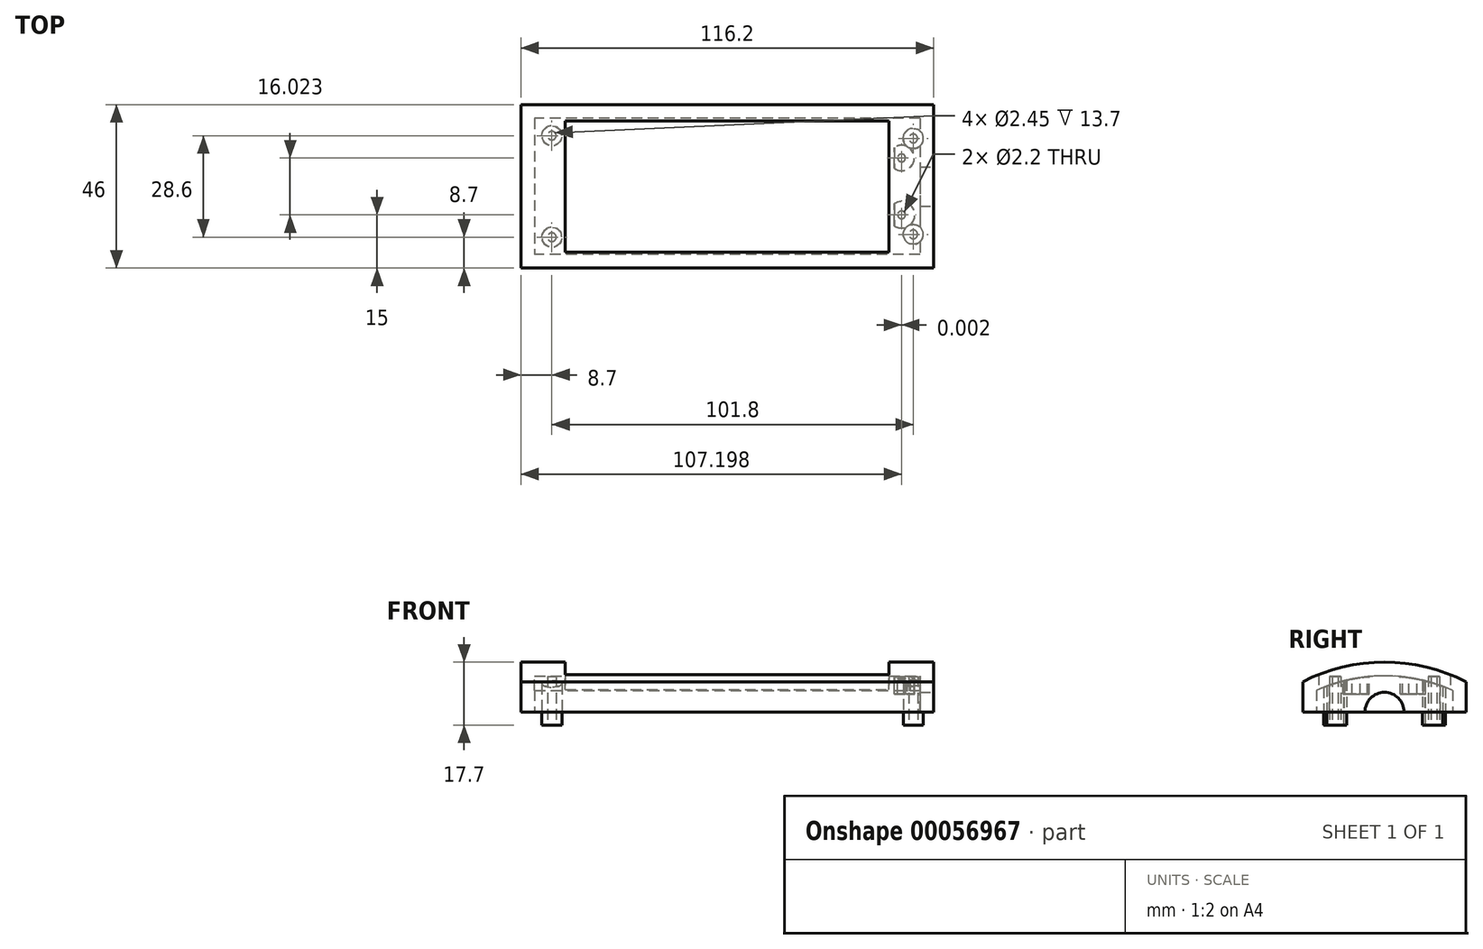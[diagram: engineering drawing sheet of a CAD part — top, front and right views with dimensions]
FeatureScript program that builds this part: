
annotation { "Feature Type Name" : "Feature", "Feature Type Description" : "" }
export const myFeature = defineFeature(function(context is Context, id is Id, definition is map)
    precondition{}
    {
        {
            var Q0;
            Q0=qCreatedBy(makeId("Top.planeOp"),FACE);
            var sketch = newSketch(context, id + "F0", { "sketchPlane" : qUnion([Q0])});
            skLineSegment(sketch, "E0.rect.bottom", {"start": v(58.1, 23) * mm, "end": v(-58.1, 23) * mm});
            skLineSegment(sketch, "E0.rect.top", {"start": v(58.1, -23) * mm, "end": v(-58.1, -23) * mm});
            skLineSegment(sketch, "E0.rect.left", {"start": v(58.1, 23) * mm, "end": v(58.1, -23) * mm});
            skLineSegment(sketch, "E0.rect.right", {"start": v(-58.1, 23) * mm, "end": v(-58.1, -23) * mm});
            skPoint(sketch, "E0.rect.middle", {"position": v(0, 0) * mm});
            skLineSegment(sketch, "E1.rect.bottom", {"start": v(45.6, 18.5) * mm, "end": v(-45.6, 18.5) * mm});
            skLineSegment(sketch, "E1.rect.top", {"start": v(45.6, -18.5) * mm, "end": v(-45.6, -18.5) * mm});
            skLineSegment(sketch, "E1.rect.left", {"start": v(45.6, 18.5) * mm, "end": v(45.6, -18.5) * mm});
            skLineSegment(sketch, "E1.rect.right", {"start": v(-45.6, 18.5) * mm, "end": v(-45.6, -18.5) * mm});
            skSolve(sketch);
        }
        {
            var Q0;
            Q0=makeQuery(id+"F0.imprint","IMPRINT",FACE,{"disambiguationData":[TD([[makeQuery(id+"F0.imprint","IMPRINT",EDGE,{"derivedFrom":sQuery(id+"F0.wireOp",EDGE,"E0.rect.bottom")}),1.0]])]});
            var Q1;
            Q1=makeQuery(id+"F0.imprint","IMPRINT",FACE,{"disambiguationData":[TD([[makeQuery(id+"F0.imprint","IMPRINT",EDGE,{"derivedFrom":sQuery(id+"F0.wireOp",EDGE,"E1.rect.bottom")}),1.0]])]});
            extrude(context, id + "F1", {"entities" : qUnion([Q0, Q1]), "depth" : 14 * mm});
        }
        {
            var Q0;
            Q0=makeQuery(id+"F1.opExtrude","SWEPT_FACE",FACE,{"disambiguationData":[OSD([sQuery(id+"F0.wireOp",EDGE,"E0.rect.left")])]});
            var sketch = newSketch(context, id + "F2", { "sketchPlane" : qUnion([Q0])});
            skLineSegment(sketch, "E2", {"start": v(-23, 0) * mm, "end": v(-23, 8.5) * mm, "construction": true});
            skLineSegment(sketch, "E3", {"start": v(-23, 8.5) * mm, "end": v(23, 8.5) * mm, "construction": true});
            skLineSegment(sketch, "E4", {"start": v(23, 8.5) * mm, "end": v(23, 0) * mm, "construction": true});
            skLineSegment(sketch, "E5", {"start": v(23, 0) * mm, "end": v(-23, 0) * mm, "construction": true});
            skLineSegment(sketch, "E6.0", {"start": v(23, 14) * mm, "end": v(-23, 14) * mm, "construction": true});
            skLineSegment(sketch, "E7", {"start": v(0, 8.5) * mm, "end": v(0, 15.93) * mm, "construction": true});
            skPoint(sketch, "E7.endSnap0", {"position": v(0, 14) * mm});
            skArc(sketch, "E8", {"start": v(23, 8.5) * mm, "mid": v(0, 14) * mm, "end": v(-23, 8.5) * mm});
            skLineSegment(sketch, "E9", {"start": v(-23, 8.5) * mm, "end": v(-26.27, 8.5) * mm});
            skLineSegment(sketch, "E10", {"start": v(-26.27, 8.5) * mm, "end": v(-26.27, 18.5) * mm});
            skLineSegment(sketch, "E11", {"start": v(-26.27, 18.5) * mm, "end": v(26.97, 18.5) * mm});
            skLineSegment(sketch, "E12", {"start": v(26.97, 18.5) * mm, "end": v(26.97, 8.2) * mm});
            skLineSegment(sketch, "E13", {"start": v(26.97, 8.2) * mm, "end": v(23, 8.5) * mm});
            skSolve(sketch);
        }
        {
            var Q0;
            {var subQ4=sQuery(id+"F2.wireOp",EDGE,"E9");Q0=makeQuery(id+"F2.imprint","IMPRINT",FACE,{"disambiguationData":[TD([[makeQuery(id+"F2.imprint","IMPRINT",EDGE,{"derivedFrom":subQ4}),-1.0]])]});}
            var Q1;
            {var subQ0=sQuery(id+"F2.wireOp",EDGE,"E8");var subQ1=sQuery(id+"F0.wireOp",EDGE,"E0.rect.left");var subQ4=makeQuery(id+"F1.opExtrude","CAP_EDGE",EDGE,{"disambiguationData":[OSD([subQ1])],"isStart":false});var subQ5=makeQuery(id+"F2.imprint","INTERSECT",VERTEX,{"derivedFrom":[subQ4,subQ0]});Q1=makeQuery(id+"F2.imprint","IMPRINT",FACE,{"disambiguationData":[TD([[makeQuery(id+"F2.imprint","IMPRINT",EDGE,{"disambiguationData":[TD([[subQ5,-1.0]])],"derivedFrom":subQ4}),1.0]])]});}
            var Q2;
            {var subQ0=sQuery(id+"F2.wireOp",EDGE,"E8");var subQ1=sQuery(id+"F0.wireOp",EDGE,"E0.rect.left");var subQ4=makeQuery(id+"F1.opExtrude","CAP_EDGE",EDGE,{"disambiguationData":[OSD([subQ1])],"isStart":false});var subQ5=makeQuery(id+"F2.imprint","INTERSECT",VERTEX,{"derivedFrom":[subQ4,subQ0]});Q2=makeQuery(id+"F2.imprint","IMPRINT",FACE,{"disambiguationData":[TD([[makeQuery(id+"F2.imprint","IMPRINT",EDGE,{"disambiguationData":[TD([[subQ5,1.0]])],"derivedFrom":subQ4}),1.0]])]});}
            extrude(context, id + "F3", {"entities" : qUnion([Q0, Q1, Q2]), "operationType" : NewBodyOperationType.REMOVE, "endBound" : BoundingType.THROUGH_ALL, "oppositeDirection" : true, "depth" : 25 * mm});
        }
        {
            var Q0;
            Q0=makeQuery(id+"F1.opExtrude","CAP_FACE",FACE,{"disambiguationData":[OSD([sQuery(id+"F0.wireOp",EDGE,"E0.rect.bottom"),sQuery(id+"F0.wireOp",EDGE,"E0.rect.top"),sQuery(id+"F0.wireOp",EDGE,"E0.rect.left"),sQuery(id+"F0.wireOp",EDGE,"E0.rect.right")])],"isStart":true});
            shell(context, id + "F4", {"entities" : qUnion([Q0]), "thickness" : 3.85 * mm});
        }
        {
            var Q0;
            Q0=qCreatedBy(makeId("Top.planeOp"),FACE);
            var sketch = newSketch(context, id + "F5", { "sketchPlane" : qUnion([Q0])});
            skPoint(sketch, "E14.4", {"position": v(0, 0) * mm});
            skLineSegment(sketch, "E14.5", {"start": v(45.6, 18.5) * mm, "end": v(-45.6, 18.5) * mm});
            skLineSegment(sketch, "E14.6", {"start": v(45.6, -18.5) * mm, "end": v(-45.6, -18.5) * mm});
            skLineSegment(sketch, "E14.7", {"start": v(45.6, 18.5) * mm, "end": v(45.6, -18.5) * mm});
            skLineSegment(sketch, "E14.8", {"start": v(-45.6, 18.5) * mm, "end": v(-45.6, -18.5) * mm});
            skPoint(sketch, "E14.9", {"position": v(0, 0) * mm});
            skSolve(sketch);
        }
        {
            var Q0;
            Q0=makeQuery(id+"F5.imprint","IMPRINT",FACE,{"disambiguationData":[TD([[makeQuery(id+"F5.imprint","IMPRINT",EDGE,{"derivedFrom":sQuery(id+"F5.wireOp",EDGE,"E14.5")}),1.0]])]});
            extrude(context, id + "F6", {"entities" : qUnion([Q0]), "operationType" : NewBodyOperationType.REMOVE, "endBound" : BoundingType.THROUGH_ALL, "depth" : 25 * mm});
        }
        {
            var Q0;
            Q0=makeQuery(id+"F1.opExtrude","CAP_FACE",FACE,{"disambiguationData":[OSD([sQuery(id+"F0.wireOp",EDGE,"E0.rect.bottom"),sQuery(id+"F0.wireOp",EDGE,"E0.rect.top"),sQuery(id+"F0.wireOp",EDGE,"E0.rect.left"),sQuery(id+"F0.wireOp",EDGE,"E0.rect.right")])],"isStart":true});
            var sketch = newSketch(context, id + "F7", { "sketchPlane" : qUnion([Q0])});
            skLineSegment(sketch, "E15.bottom", {"start": v(-58.1, 23) * mm, "end": v(-49.4, 23) * mm, "construction": true});
            skLineSegment(sketch, "E15.top", {"start": v(-58.1, 14.3) * mm, "end": v(-49.4, 14.3) * mm, "construction": true});
            skLineSegment(sketch, "E15.left", {"start": v(-58.1, 23) * mm, "end": v(-58.1, 14.3) * mm, "construction": true});
            skLineSegment(sketch, "E15.right", {"start": v(-49.4, 23) * mm, "end": v(-49.4, 14.3) * mm, "construction": true});
            skCircle(sketch, "E16", {"center": v(-49.4, 14.3) * mm, "radius": 2.8 * mm});
            skLineSegment(sketch, "E17.bottom", {"start": v(-58.1, -23) * mm, "end": v(-49.4, -23) * mm, "construction": true});
            skLineSegment(sketch, "E17.top", {"start": v(-58.1, -14.3) * mm, "end": v(-49.4, -14.3) * mm, "construction": true});
            skLineSegment(sketch, "E17.left", {"start": v(-58.1, -23) * mm, "end": v(-58.1, -14.3) * mm, "construction": true});
            skLineSegment(sketch, "E17.right", {"start": v(-49.4, -23) * mm, "end": v(-49.4, -14.3) * mm, "construction": true});
            skCircle(sketch, "E18", {"center": v(-49.4, -14.3) * mm, "radius": 2.8 * mm});
            skLineSegment(sketch, "E19.bottom", {"start": v(58.1, 23) * mm, "end": v(52.4, 23) * mm, "construction": true});
            skLineSegment(sketch, "E19.top", {"start": v(58.1, 13.5) * mm, "end": v(52.4, 13.5) * mm, "construction": true});
            skLineSegment(sketch, "E19.left", {"start": v(58.1, 23) * mm, "end": v(58.1, 13.5) * mm, "construction": true});
            skLineSegment(sketch, "E19.right", {"start": v(52.4, 23) * mm, "end": v(52.4, 13.5) * mm, "construction": true});
            skCircle(sketch, "E20", {"center": v(52.4, 13.5) * mm, "radius": 2.8 * mm});
            skLineSegment(sketch, "E21.bottom", {"start": v(58.1, -23) * mm, "end": v(52.4, -23) * mm, "construction": true});
            skLineSegment(sketch, "E21.top", {"start": v(58.1, -13.5) * mm, "end": v(52.4, -13.5) * mm, "construction": true});
            skLineSegment(sketch, "E21.left", {"start": v(58.1, -23) * mm, "end": v(58.1, -13.5) * mm, "construction": true});
            skLineSegment(sketch, "E21.right", {"start": v(52.4, -23) * mm, "end": v(52.4, -13.5) * mm, "construction": true});
            skCircle(sketch, "E22", {"center": v(52.4, -13.5) * mm, "radius": 2.85 * mm});
            skSolve(sketch);
        }
        {
            var Q0;
            Q0 = qSketchRegion(id + "F7", true);
            var Q1;
            Q1=makeQuery(id+"F4.opShell","OFFSET_FACE",FACE,{"disambiguationData":[OSD([sQuery(id+"F2.wireOp",EDGE,"E8")])]});
            extrude(context, id + "F8", {"entities" : qUnion([Q0]), "operationType" : NewBodyOperationType.ADD, "endBound" : BoundingType.UP_TO_SURFACE, "oppositeDirection" : true, "endBoundEntityFace" : qUnion([Q1]), "depth" : 25 * mm});
        }
        {
            var Q0;
            Q0=makeQuery(id+"F1.opExtrude","SWEPT_FACE",FACE,{"disambiguationData":[OSD([sQuery(id+"F0.wireOp",EDGE,"E0.rect.left")])]});
            var sketch = newSketch(context, id + "F9", { "sketchPlane" : qUnion([Q0])});
            skCircle(sketch, "E23", {"center": v(0, 0) * mm, "radius": 5.5 * mm});
            skSolve(sketch);
        }
        {
            var Q0;
            {var subQ0=sQuery(id+"F9.wireOp",EDGE,"E23");var subQ1=makeQuery(id+"F1.opExtrude","CAP_EDGE",EDGE,{"disambiguationData":[OSD([sQuery(id+"F0.wireOp",EDGE,"E0.rect.left")])],"isStart":true});var subQ2=makeQuery(id+"F9.imprint","INTERSECT",VERTEX,{"disambiguationData":[OD(0.0)],"derivedFrom":[subQ1,subQ0]});Q0=makeQuery(id+"F9.imprint","IMPRINT",FACE,{"disambiguationData":[TD([[makeQuery(id+"F9.imprint","IMPRINT",EDGE,{"disambiguationData":[TD([[subQ2,1.0]])],"derivedFrom":subQ0}),1.0]])]});}
            var Q1;
            {var subQ0=sQuery(id+"F9.wireOp",EDGE,"E23");var subQ1=makeQuery(id+"F1.opExtrude","CAP_EDGE",EDGE,{"disambiguationData":[OSD([sQuery(id+"F0.wireOp",EDGE,"E0.rect.left")])],"isStart":true});var subQ2=makeQuery(id+"F9.imprint","INTERSECT",VERTEX,{"disambiguationData":[OD(0.0)],"derivedFrom":[subQ1,subQ0]});Q1=makeQuery(id+"F9.imprint","IMPRINT",FACE,{"disambiguationData":[TD([[makeQuery(id+"F9.imprint","IMPRINT",EDGE,{"disambiguationData":[TD([[subQ2,-1.0]])],"derivedFrom":subQ0}),1.0]])]});}
            extrude(context, id + "F10", {"entities" : qUnion([Q0, Q1]), "operationType" : NewBodyOperationType.REMOVE, "oppositeDirection" : true, "depth" : 25 * mm});
        }
        {
            var Q0;
            Q0=makeQuery(id+"F8.boolean.opBoolean","MERGE",FACE,{"derivedFrom":[makeQuery(id+"F1.opExtrude","CAP_FACE",FACE,{"disambiguationData":[OSD([sQuery(id+"F0.wireOp",EDGE,"E0.rect.bottom"),sQuery(id+"F0.wireOp",EDGE,"E0.rect.top"),sQuery(id+"F0.wireOp",EDGE,"E0.rect.left"),sQuery(id+"F0.wireOp",EDGE,"E0.rect.right")])],"isStart":true}),makeQuery(id+"F8.opExtrude","CAP_FACE",FACE,{"disambiguationData":[OSD([sQuery(id+"F7.wireOp",EDGE,"E20")])],"isStart":true}),makeQuery(id+"F8.opExtrude","CAP_FACE",FACE,{"disambiguationData":[OSD([sQuery(id+"F7.wireOp",EDGE,"E22")])],"isStart":true})]});
            var sketch = newSketch(context, id + "F11", { "sketchPlane" : qUnion([Q0])});
            skCircle(sketch, "E24.0", {"center": v(-49.4, 14.3) * mm, "radius": 2.8 * mm, "construction": true});
            skCircle(sketch, "E24.1", {"center": v(-49.4, -14.3) * mm, "radius": 2.8 * mm, "construction": true});
            skArc(sketch, "E24.2", {"start": v(54.25, 15.6) * mm, "mid": v(49.6, 13.5) * mm, "end": v(54.25, 11.4) * mm, "construction": true});
            skArc(sketch, "E24.3", {"start": v(54.25, -11.33) * mm, "mid": v(49.55, -13.5) * mm, "end": v(54.25, -15.67) * mm, "construction": true});
            skCircle(sketch, "E25", {"center": v(-49.4, 14.3) * mm, "radius": 1.23 * mm});
            skCircle(sketch, "E26", {"center": v(-49.4, -14.3) * mm, "radius": 1.23 * mm});
            skCircle(sketch, "E27", {"center": v(52.4, 13.5) * mm, "radius": 1.23 * mm});
            skCircle(sketch, "E28", {"center": v(52.4, -13.5) * mm, "radius": 1.23 * mm});
            skSolve(sketch);
        }
        {
            var Q0;
            Q0 = qSketchRegion(id + "F11", true);
            extrude(context, id + "F12", {"entities" : qUnion([Q0]), "operationType" : NewBodyOperationType.REMOVE, "oppositeDirection" : true, "depth" : 10 * mm});
        }
        {
            var Q0;
            Q0=makeQuery(id+"F8.boolean.opBoolean","MERGE",FACE,{"derivedFrom":[makeQuery(id+"F1.opExtrude","CAP_FACE",FACE,{"disambiguationData":[OSD([sQuery(id+"F0.wireOp",EDGE,"E0.rect.bottom"),sQuery(id+"F0.wireOp",EDGE,"E0.rect.top"),sQuery(id+"F0.wireOp",EDGE,"E0.rect.left"),sQuery(id+"F0.wireOp",EDGE,"E0.rect.right")])],"isStart":true}),makeQuery(id+"F8.opExtrude","CAP_FACE",FACE,{"disambiguationData":[OSD([sQuery(id+"F7.wireOp",EDGE,"E20")])],"isStart":true}),makeQuery(id+"F8.opExtrude","CAP_FACE",FACE,{"disambiguationData":[OSD([sQuery(id+"F7.wireOp",EDGE,"E22")])],"isStart":true})]});
            cPlane(context, id + "F13", {"entities" : qUnion([Q0]), "cplaneType" : CPlaneType.OFFSET, "offset" : 8 * mm, "oppositeDirection" : true, "width" : 150 * mm, "height" : 150 * mm});
        }
        {
            var Q0;
            Q0=qCreatedBy(id+"F13.planeOp",FACE);
            var sketch = newSketch(context, id + "F14", { "sketchPlane" : qUnion([Q0])});
            skPoint(sketch, "E29.0", {"position": v(58.1, 23) * mm});
            skLineSegment(sketch, "E30", {"start": v(58.1, 23) * mm, "end": v(58.1, 8) * mm, "construction": true});
            skLineSegment(sketch, "E31", {"start": v(58.1, 8) * mm, "end": v(49.1, 8) * mm, "construction": true});
            skCircle(sketch, "E32.0", {"center": v(52.4, 13.5) * mm, "radius": 1.23 * mm, "construction": true});
            skLineSegment(sketch, "E33", {"start": v(52.4, 13.5) * mm, "end": v(52.4, 8) * mm, "construction": true});
            skArc(sketch, "E34", {"start": v(47.1, 4.86) * mm, "mid": v(52.82, 8) * mm, "end": v(47.1, 11.14) * mm});
            skCircle(sketch, "E35", {"center": v(49.1, 8) * mm, "radius": 1.1 * mm});
            skLineSegment(sketch, "E36", {"start": v(47.1, 11.14) * mm, "end": v(47.1, 4.86) * mm});
            skPoint(sketch, "E37.0", {"position": v(58.1, -23) * mm});
            skLineSegment(sketch, "E38.bottom", {"start": v(58.1, -23) * mm, "end": v(49.1, -23) * mm, "construction": true});
            skLineSegment(sketch, "E38.top", {"start": v(58.1, -8) * mm, "end": v(49.1, -8) * mm, "construction": true});
            skLineSegment(sketch, "E38.left", {"start": v(58.1, -23) * mm, "end": v(58.1, -8) * mm, "construction": true});
            skLineSegment(sketch, "E38.right", {"start": v(49.1, -23) * mm, "end": v(49.1, -8) * mm, "construction": true});
            skLineSegment(sketch, "E39", {"start": v(47.1, -5.05) * mm, "end": v(47.1, -11) * mm});
            skArc(sketch, "E40", {"start": v(47.1, -11) * mm, "mid": v(52.68, -8.02) * mm, "end": v(47.1, -5.05) * mm});
            skCircle(sketch, "E41", {"center": v(49.1, -8.02) * mm, "radius": 1.1 * mm});
            skSolve(sketch);
        }
        {
            var Q0;
            Q0 = qSketchRegion(id + "F14", true);
            extrude(context, id + "F15", {"entities" : qUnion([Q0]), "operationType" : NewBodyOperationType.ADD, "depth" : 3 * mm, "hasSecondDirection" : true, "secondDirectionBound" : SecondDirectionBoundingType.UP_TO_NEXT, "secondDirectionOppositeDirection" : true, "secondDirectionDepth" : 25 * mm});
        }
        {
            var Q0;
            Q0=makeQuery(id+"F8.boolean.opBoolean","MERGE",FACE,{"derivedFrom":[makeQuery(id+"F1.opExtrude","CAP_FACE",FACE,{"disambiguationData":[OSD([sQuery(id+"F0.wireOp",EDGE,"E0.rect.bottom"),sQuery(id+"F0.wireOp",EDGE,"E0.rect.top"),sQuery(id+"F0.wireOp",EDGE,"E0.rect.left"),sQuery(id+"F0.wireOp",EDGE,"E0.rect.right")])],"isStart":true}),makeQuery(id+"F8.opExtrude","CAP_FACE",FACE,{"disambiguationData":[OSD([sQuery(id+"F7.wireOp",EDGE,"E20")])],"isStart":true}),makeQuery(id+"F8.opExtrude","CAP_FACE",FACE,{"disambiguationData":[OSD([sQuery(id+"F7.wireOp",EDGE,"E22")])],"isStart":true})]});
            var sketch = newSketch(context, id + "F16", { "sketchPlane" : qUnion([Q0])});
            skArc(sketch, "E42.0", {"start": v(54.25, 15.6) * mm, "mid": v(49.6, 13.5) * mm, "end": v(54.25, 11.4) * mm});
            skCircle(sketch, "E42.1", {"center": v(52.4, 13.5) * mm, "radius": 1.23 * mm});
            skCircle(sketch, "E42.2", {"center": v(52.4, -13.5) * mm, "radius": 1.23 * mm});
            skArc(sketch, "E42.3", {"start": v(54.25, -11.33) * mm, "mid": v(49.55, -13.5) * mm, "end": v(54.25, -15.67) * mm});
            skCircle(sketch, "E42.4", {"center": v(-49.4, 14.3) * mm, "radius": 2.8 * mm});
            skCircle(sketch, "E42.5", {"center": v(-49.4, 14.3) * mm, "radius": 1.23 * mm});
            skCircle(sketch, "E42.6", {"center": v(-49.4, -14.3) * mm, "radius": 1.23 * mm});
            skCircle(sketch, "E42.7", {"center": v(-49.4, -14.3) * mm, "radius": 2.8 * mm});
            skArc(sketch, "E43", {"start": v(54.25, 15.6) * mm, "mid": v(55.2, 13.5) * mm, "end": v(54.25, 11.4) * mm});
            skArc(sketch, "E44", {"start": v(54.25, -11.33) * mm, "mid": v(55.25, -13.5) * mm, "end": v(54.25, -15.67) * mm});
            skSolve(sketch);
        }
        {
            var Q0;
            Q0 = qSketchRegion(id + "F16", true);
            extrude(context, id + "F17", {"entities" : qUnion([Q0]), "operationType" : NewBodyOperationType.ADD, "depth" : 3.7 * mm});
        }
    });
